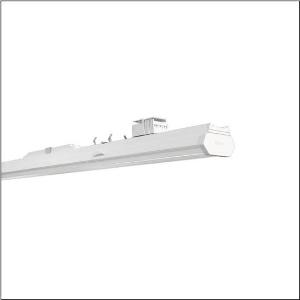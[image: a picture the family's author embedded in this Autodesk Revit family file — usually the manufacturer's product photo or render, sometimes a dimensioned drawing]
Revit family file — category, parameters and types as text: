
# Revit family: licross_r__21_protected_ho_52tp12dn4e5m3s4_92a6
name_source: partatom
category: Lighting Fixtures
units: mm (PartAtom-declared; Revit-internal decimal feet)

## family parameters
Cut with Voids When Loaded = No
Host = Face
Light Source = No
Part Type = Normal
Room Calculation Point = No
Round Connector Dimension = Use Diameter
Shared = No

## types (1)
- --- (1 x LED, 910 lm, 7.6 W, 4000K)
    Apparent Load = 8 VA
    CIE Flux Codes = 70 91 97 98 100
    Color Rendering = 80
    Color Temperature = 4000K
    Default Elevation = 1800 mm
    Description = Licross® 21 Protected HO, luminaire insert, of sheet steel, galvanised, coil coated, white, length: 1.500mm, width: 90mm, height: 103mm, LED rated luminous flux: 14.690lm, light colour: 840, SDCM (Standard Deviation of Colour Matching)MacAdam ≤ 3 SDCM (initial), control gear: DALI 2, with plug, 6-pole, with phase selection, for trunking rail, 9 or 11-core, mains connection: 220..240V, AC, 50/60Hz, rated input power: 89W, for trunking rail, 9-/11-core, internal wiring halogen-free, for emergency light function, converter,control gear: single battery element, battery: LiFePO4, 9Ah, primary light control with lens, of plastic, primary optical cover: cover, of PMMA, light emission: direct distribution, primary light characteristic: symmetric, protection rating (complete): IP64, insulation class (complete): insulation class I (protective earthing), certification: CE, UKCA, protection symbol: D if used in an environment with conductive dust loads with corresponding accessories, impact resistance: IK06, permissible ambient temperature for indoor applications: +5..+30°C, standard: EN 60598-2-22, LABS conformity tested according to VDMA 24364:2018-05, reducing of maximum allowable ambient temperature of 5°C with ceiling mounting, corresponds to IFS (International Featured Standards) requirements for safety and quality in the food industry, packaging unit: 1 piece
    Height = 92 mm
    Lamp = 1 x LED
    Lamp Light Flux = 910 lm
    Lamp Power = 7.6 W
    Lamp count = 1
    Length = 1500 mm
    Luminous efficacy = 120 lm/W
    Manufacturer = Siteco
    ModVariant = No
    Model = 52TP12DN4E5M3S4
    Mounting Place = Ceiling
    Mounting Type = Pendant
    Number of Poles = 1
    OnlyDefault = Yes
    Power Factor = 1
    Product Name = Licross® 21 Protected HO
    Product group = luminaire insert | ceiling pendant
    ProductGroupID = 901
    Protection Class = Protection class I
    Protection Degree = IP 64
    RLX_Detail_Level = 1
    RLX_Emergency_Light_Flux = 0 lm
    RLX_Emergency_Type = 0
    RLX_Emergency_Type_DB = No
    RlxData = <blob elided: 24949 chars, md5=9e55000a>
    Socket = socket
    Standby Power = 0 W
    System Light Flux = 910 lm
    System Power = 8 W
    Type Comments = : emergency light operation: 3 h
    Type Image = l_1256148.jpg
    URL = http://relux.com
    VarID = @adj_115127
    Voltage = 0 V
    Weight = 0.00 kg
    Width = 88 mm

## geometry (parser evidence)
native form markers: Blend x4, Sweep x12
no freeform markers — native parametric forms only
